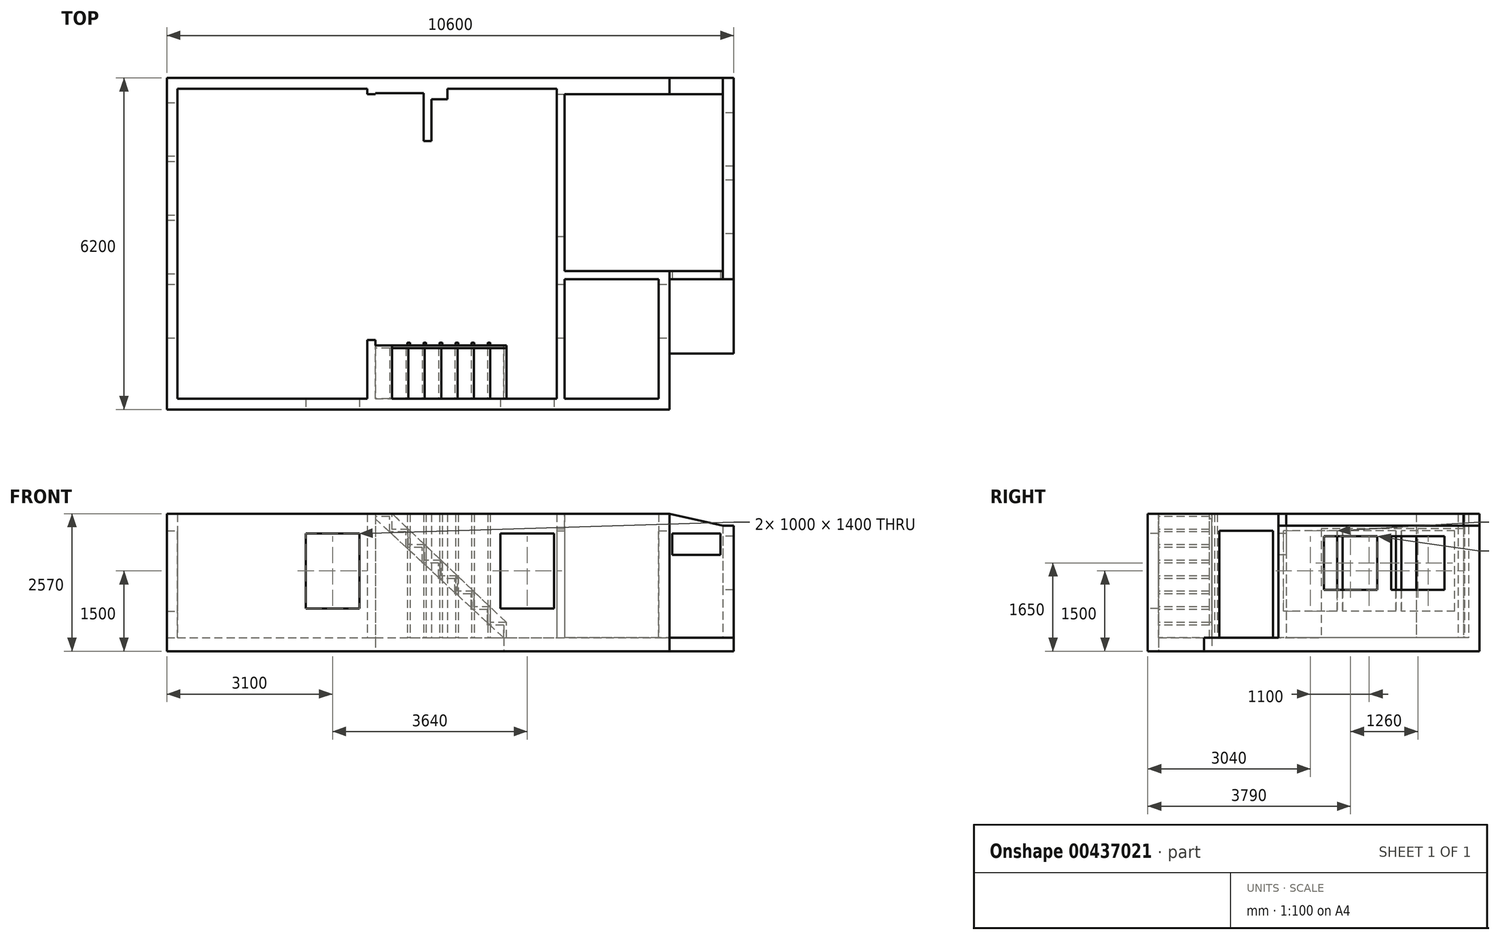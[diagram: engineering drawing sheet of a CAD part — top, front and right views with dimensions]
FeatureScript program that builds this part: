
annotation { "Feature Type Name" : "Feature", "Feature Type Description" : "" }
export const myFeature = defineFeature(function(context is Context, id is Id, definition is map)
    precondition{}
    {
        {
            var Q0;
            Q0=qCreatedBy(makeId("Top.planeOp"),FACE);
            var sketch = newSketch(context, id + "F0", { "sketchPlane" : qUnion([Q0])});
            skLineSegment(sketch, "E0.bottom", {"start": v(0, 0) * mm, "end": v(10600, 0) * mm});
            skLineSegment(sketch, "E0.top", {"start": v(0, -6200) * mm, "end": v(9400, -6200) * mm});
            skLineSegment(sketch, "E0.left", {"start": v(0, 0) * mm, "end": v(0, -6200) * mm});
            skLineSegment(sketch, "E0.right", {"start": v(10600, 0) * mm, "end": v(10600, -5150) * mm});
            skLineSegment(sketch, "E1.top", {"start": v(10600, -5150) * mm, "end": v(9400, -5150) * mm});
            skLineSegment(sketch, "E1.right", {"start": v(9400, -6200) * mm, "end": v(9400, -5150) * mm});
            skLineSegment(sketch, "E2.top", {"start": v(3900, -5000) * mm, "end": v(6300, -5000) * mm});
            skLineSegment(sketch, "E2.left", {"start": v(3900, -6000) * mm, "end": v(3900, -5000) * mm});
            skLineSegment(sketch, "E2.right", {"start": v(6300, -6000) * mm, "end": v(6300, -5000) * mm});
            skLineSegment(sketch, "E3.top", {"start": v(3900, -6000) * mm, "end": v(6300, -6000) * mm});
            skSolve(sketch);
        }
        {
            var Q0;
            Q0=qSketchRegion(id+"F0",true);
            extrude(context, id + "F1", {"entities" : qUnion([Q0]), "depth" : 250 * mm});
        }
        {
            var Q0;
            Q0=makeQuery(id+"F1.opExtrude","CAP_FACE",FACE,{"disambiguationData":[OSD([sQuery(id+"F0.wireOp",EDGE,"E0.bottom"),sQuery(id+"F0.wireOp",EDGE,"E0.top"),sQuery(id+"F0.wireOp",EDGE,"E0.left"),sQuery(id+"F0.wireOp",EDGE,"E0.right")])],"isStart":false});
            var sketch = newSketch(context, id + "F2", { "sketchPlane" : qUnion([Q0])});
            skLineSegment(sketch, "E4.bottom", {"start": v(200, -200) * mm, "end": v(3750, -200) * mm});
            skLineSegment(sketch, "E4.top", {"start": v(200, -6000) * mm, "end": v(3750, -6000) * mm});
            skLineSegment(sketch, "E4.left", {"start": v(200, -200) * mm, "end": v(200, -6000) * mm});
            skLineSegment(sketch, "E4.right", {"start": v(10400, -300) * mm, "end": v(10400, -3610) * mm});
            skLineSegment(sketch, "E5.bottom", {"start": v(9200, -6000) * mm, "end": v(7440, -6000) * mm});
            skLineSegment(sketch, "E5.top", {"start": v(10400, -3610) * mm, "end": v(7440, -3610) * mm});
            skLineSegment(sketch, "E6.top", {"start": v(3750, -4900) * mm, "end": v(3900, -4900) * mm});
            skLineSegment(sketch, "E6.left", {"start": v(3750, -6000) * mm, "end": v(3750, -4900) * mm});
            skLineSegment(sketch, "E6.right", {"start": v(3900, -6000) * mm, "end": v(3900, -4900) * mm});
            skLineSegment(sketch, "E7.top", {"start": v(3750, -300) * mm, "end": v(3900, -300) * mm});
            skLineSegment(sketch, "E7.left", {"start": v(3750, -200) * mm, "end": v(3750, -300) * mm});
            skLineSegment(sketch, "E7.right", {"start": v(3900, -280) * mm, "end": v(3900, -300) * mm});
            skLineSegment(sketch, "E8.top", {"start": v(4800, -1180) * mm, "end": v(4950, -1180) * mm});
            skLineSegment(sketch, "E8.left", {"start": v(4800, -280) * mm, "end": v(4800, -1180) * mm});
            skLineSegment(sketch, "E8.right", {"start": v(4950, -400) * mm, "end": v(4950, -1180) * mm});
            skLineSegment(sketch, "E9.top", {"start": v(7290, -300) * mm, "end": v(7440, -300) * mm});
            skLineSegment(sketch, "E9.left", {"start": v(7290, -200) * mm, "end": v(7290, -300) * mm});
            skLineSegment(sketch, "E10.top", {"start": v(9200, -3760) * mm, "end": v(7440, -3760) * mm});
            skLineSegment(sketch, "E10.right", {"start": v(7440, -6000) * mm, "end": v(7440, -3760) * mm});
            skLineSegment(sketch, "E11.top", {"start": v(7290, -2960) * mm, "end": v(7440, -2960) * mm});
            skLineSegment(sketch, "E11.left", {"start": v(7290, -6000) * mm, "end": v(7290, -2960) * mm});
            skLineSegment(sketch, "E11.right", {"start": v(7440, -3610) * mm, "end": v(7440, -2960) * mm});
            skLineSegment(sketch, "E12.bottom", {"start": v(0, 0) * mm, "end": v(10600, 0) * mm});
            skLineSegment(sketch, "E12.top", {"start": v(0, -6200) * mm, "end": v(9400, -6200) * mm});
            skLineSegment(sketch, "E12.left", {"start": v(0, 0) * mm, "end": v(0, -6200) * mm});
            skLineSegment(sketch, "E12.right", {"start": v(10600, 0) * mm, "end": v(10600, -3760) * mm});
            skLineSegment(sketch, "E13.trimOffspring", {"start": v(5250, -200) * mm, "end": v(7290, -200) * mm});
            skLineSegment(sketch, "E14.trimOffspring", {"start": v(3900, -6000) * mm, "end": v(7290, -6000) * mm});
            skLineSegment(sketch, "E15.top", {"start": v(4950, -400) * mm, "end": v(5250, -400) * mm});
            skLineSegment(sketch, "E15.right", {"start": v(5250, -200) * mm, "end": v(5250, -400) * mm});
            skLineSegment(sketch, "E16.top", {"start": v(3900, -280) * mm, "end": v(4800, -280) * mm});
            skLineSegment(sketch, "E17.trimOffspring", {"start": v(7440, -6000) * mm, "end": v(9200, -6000) * mm});
            skLineSegment(sketch, "E18.trimOffspring", {"start": v(9200, -3760) * mm, "end": v(9200, -6000) * mm});
            skLineSegment(sketch, "E19", {"start": v(10600, -3760) * mm, "end": v(9400, -3760) * mm});
            skLineSegment(sketch, "E20", {"start": v(9400, -3760) * mm, "end": v(9400, -6200) * mm});
            skLineSegment(sketch, "E21", {"start": v(7440, -300) * mm, "end": v(10400, -300) * mm});
            skSolve(sketch);
        }
        {
            var Q0;
            Q0=qSketchRegion(id+"F2",true);
            extrude(context, id + "F3", {"entities" : qUnion([Q0]), "operationType" : NewBodyOperationType.ADD, "depth" : 2320 * mm});
        }
        {
            var Q0;
            Q0=makeQuery(id+"F3.boolean.opBoolean","MERGE",FACE,{"derivedFrom":[makeQuery(id+"F1.opExtrude","SWEPT_FACE",FACE,{"disambiguationData":[OSD([sQuery(id+"F0.wireOp",EDGE,"E1.right")])]}),makeQuery(id+"F3.opExtrude","SWEPT_FACE",FACE,{"disambiguationData":[OSD([sQuery(id+"F2.wireOp",EDGE,"E20")])]})]});
            var sketch = newSketch(context, id + "F4", { "sketchPlane" : qUnion([Q0])});
            skLineSegment(sketch, "E22.bottom", {"start": v(-4860, 250) * mm, "end": v(-3860, 250) * mm});
            skLineSegment(sketch, "E22.top", {"start": v(-4860, 2250) * mm, "end": v(-3860, 2250) * mm});
            skLineSegment(sketch, "E22.left", {"start": v(-4860, 250) * mm, "end": v(-4860, 2250) * mm});
            skLineSegment(sketch, "E22.right", {"start": v(-3860, 250) * mm, "end": v(-3860, 2250) * mm});
            skSolve(sketch);
        }
        {
            var Q0;
            Q0=qSketchRegion(id+"F4",true);
            extrude(context, id + "F5", {"entities" : qUnion([Q0]), "operationType" : NewBodyOperationType.REMOVE, "endBound" : BoundingType.THROUGH_ALL, "oppositeDirection" : true, "depth" : 3000 * mm});
        }
        {
            var Q0;
            Q0=makeQuery(id+"F3.boolean.opBoolean","MERGE",FACE,{"derivedFrom":[makeQuery(id+"F1.opExtrude","SWEPT_FACE",FACE,{"disambiguationData":[OSD([sQuery(id+"F0.wireOp",EDGE,"E0.top")])]}),makeQuery(id+"F3.opExtrude","SWEPT_FACE",FACE,{"disambiguationData":[OSD([sQuery(id+"F2.wireOp",EDGE,"E12.top")])]})]});
            var sketch = newSketch(context, id + "F6", { "sketchPlane" : qUnion([Q0])});
            skLineSegment(sketch, "E23.bottom", {"start": v(7240, 2200) * mm, "end": v(6240, 2200) * mm});
            skLineSegment(sketch, "E23.top", {"start": v(7240, 800) * mm, "end": v(6240, 800) * mm});
            skLineSegment(sketch, "E23.left", {"start": v(7240, 2200) * mm, "end": v(7240, 800) * mm});
            skLineSegment(sketch, "E23.right", {"start": v(6240, 2200) * mm, "end": v(6240, 800) * mm});
            skLineSegment(sketch, "E24.bottom", {"start": v(2600, 2200) * mm, "end": v(3600, 2200) * mm});
            skLineSegment(sketch, "E24.top", {"start": v(2600, 800) * mm, "end": v(3600, 800) * mm});
            skLineSegment(sketch, "E24.left", {"start": v(2600, 2200) * mm, "end": v(2600, 800) * mm});
            skLineSegment(sketch, "E24.right", {"start": v(3600, 2200) * mm, "end": v(3600, 800) * mm});
            skLineSegment(sketch, "E25.bottom", {"start": v(9450, 2200) * mm, "end": v(10350, 2200) * mm});
            skLineSegment(sketch, "E25.top", {"start": v(9450, 1800) * mm, "end": v(10350, 1800) * mm});
            skLineSegment(sketch, "E25.left", {"start": v(9450, 2200) * mm, "end": v(9450, 1800) * mm});
            skLineSegment(sketch, "E25.right", {"start": v(10350, 2200) * mm, "end": v(10350, 1800) * mm});
            skSolve(sketch);
        }
        {
            var Q0;
            Q0=qSketchRegion(id+"F6",true);
            var Q1;
            Q1=makeQuery(id+"F3.opExtrude","SWEPT_FACE",FACE,{"disambiguationData":[OSD([sQuery(id+"F2.wireOp",EDGE,"E9.top"),sQuery(id+"F2.wireOp",EDGE,"E21")])]});
            extrude(context, id + "F7", {"entities" : qUnion([Q0]), "operationType" : NewBodyOperationType.REMOVE, "endBound" : BoundingType.UP_TO_SURFACE, "oppositeDirection" : true, "endBoundEntityFace" : qUnion([Q1]), "depth" : 25 * mm});
        }
        {
            var Q0;
            Q0=makeQuery(id+"F3.opExtrude","SWEPT_FACE",FACE,{"disambiguationData":[OSD([sQuery(id+"F2.wireOp",EDGE,"E4.right")])]});
            var sketch = newSketch(context, id + "F8", { "sketchPlane" : qUnion([Q0])});
            skLineSegment(sketch, "E26.bottom", {"start": v(650, 2150) * mm, "end": v(1650, 2150) * mm});
            skLineSegment(sketch, "E26.top", {"start": v(650, 1150) * mm, "end": v(1650, 1150) * mm});
            skLineSegment(sketch, "E26.left", {"start": v(650, 2150) * mm, "end": v(650, 1150) * mm});
            skLineSegment(sketch, "E26.right", {"start": v(1650, 2150) * mm, "end": v(1650, 1150) * mm});
            skLineSegment(sketch, "E27.bottom", {"start": v(1910, 2150) * mm, "end": v(2910, 2150) * mm});
            skLineSegment(sketch, "E27.top", {"start": v(1910, 1150) * mm, "end": v(2910, 1150) * mm});
            skLineSegment(sketch, "E27.left", {"start": v(1910, 2150) * mm, "end": v(1910, 1150) * mm});
            skLineSegment(sketch, "E27.right", {"start": v(2910, 2150) * mm, "end": v(2910, 1150) * mm});
            skSolve(sketch);
        }
        {
            var Q0;
            Q0=qSketchRegion(id+"F8",true);
            extrude(context, id + "F9", {"entities" : qUnion([Q0]), "operationType" : NewBodyOperationType.REMOVE, "endBound" : BoundingType.UP_TO_NEXT, "oppositeDirection" : true, "depth" : 25 * mm});
        }
        {
            var Q0;
            Q0=makeQuery(id+"F3.opExtrude","SWEPT_FACE",FACE,{"disambiguationData":[OSD([sQuery(id+"F2.wireOp",EDGE,"E4.left")])]});
            var sketch = newSketch(context, id + "F10", { "sketchPlane" : qUnion([Q0])});
            skLineSegment(sketch, "E28.bottom", {"start": v(-3660, 2250) * mm, "end": v(-2660, 2250) * mm});
            skLineSegment(sketch, "E28.top", {"start": v(-3660, 750) * mm, "end": v(-2660, 750) * mm});
            skLineSegment(sketch, "E28.left", {"start": v(-3660, 2250) * mm, "end": v(-3660, 750) * mm});
            skLineSegment(sketch, "E28.right", {"start": v(-2660, 2250) * mm, "end": v(-2660, 750) * mm});
            skLineSegment(sketch, "E29.bottom", {"start": v(-2560, 2250) * mm, "end": v(-1560, 2250) * mm});
            skLineSegment(sketch, "E29.top", {"start": v(-2560, 750) * mm, "end": v(-1560, 750) * mm});
            skLineSegment(sketch, "E29.left", {"start": v(-2560, 2250) * mm, "end": v(-2560, 750) * mm});
            skLineSegment(sketch, "E29.right", {"start": v(-1560, 2250) * mm, "end": v(-1560, 750) * mm});
            skLineSegment(sketch, "E30.bottom", {"start": v(-1460, 2250) * mm, "end": v(-460, 2250) * mm});
            skLineSegment(sketch, "E30.top", {"start": v(-1460, 750) * mm, "end": v(-460, 750) * mm});
            skLineSegment(sketch, "E30.left", {"start": v(-1460, 2250) * mm, "end": v(-1460, 750) * mm});
            skLineSegment(sketch, "E30.right", {"start": v(-460, 2250) * mm, "end": v(-460, 750) * mm});
            skSolve(sketch);
        }
        {
            var Q0;
            Q0=qSketchRegion(id+"F10",true);
            extrude(context, id + "F11", {"entities" : qUnion([Q0]), "operationType" : NewBodyOperationType.REMOVE, "endBound" : BoundingType.UP_TO_NEXT, "oppositeDirection" : true, "depth" : 25 * mm});
        }
        {
            var Q0;
            Q0=makeQuery(id+"F3.opExtrude","CAP_FACE",FACE,{"disambiguationData":[OSD([sQuery(id+"F2.wireOp",EDGE,"E4.bottom"),sQuery(id+"F2.wireOp",EDGE,"E4.top"),sQuery(id+"F2.wireOp",EDGE,"E4.left"),sQuery(id+"F2.wireOp",EDGE,"E4.right"),sQuery(id+"F2.wireOp",EDGE,"E5.top"),sQuery(id+"F2.wireOp",EDGE,"E6.top"),sQuery(id+"F2.wireOp",EDGE,"E6.left"),sQuery(id+"F2.wireOp",EDGE,"E6.right"),sQuery(id+"F2.wireOp",EDGE,"E7.top"),sQuery(id+"F2.wireOp",EDGE,"E7.left"),sQuery(id+"F2.wireOp",EDGE,"E7.right"),sQuery(id+"F2.wireOp",EDGE,"E8.top"),sQuery(id+"F2.wireOp",EDGE,"E8.left"),sQuery(id+"F2.wireOp",EDGE,"E8.right"),sQuery(id+"F2.wireOp",EDGE,"E9.top"),sQuery(id+"F2.wireOp",EDGE,"E9.left"),sQuery(id+"F2.wireOp",EDGE,"E9.right"),sQuery(id+"F2.wireOp",EDGE,"E10.top"),sQuery(id+"F2.wireOp",EDGE,"E10.right"),sQuery(id+"F2.wireOp",EDGE,"E11.top"),sQuery(id+"F2.wireOp",EDGE,"E11.left"),sQuery(id+"F2.wireOp",EDGE,"E11.right"),sQuery(id+"F2.wireOp",EDGE,"E12.bottom"),sQuery(id+"F2.wireOp",EDGE,"E12.top"),sQuery(id+"F2.wireOp",EDGE,"E12.left"),sQuery(id+"F2.wireOp",EDGE,"E12.right"),sQuery(id+"F2.wireOp",EDGE,"E13.trimOffspring"),sQuery(id+"F2.wireOp",EDGE,"f96be5dc-ae23-419c-a534-e8c19ccc8482.trimOffspring"),sQuery(id+"F2.wireOp",EDGE,"E14.trimOffspring"),sQuery(id+"F2.wireOp",EDGE,"E15.top"),sQuery(id+"F2.wireOp",EDGE,"E15.right"),sQuery(id+"F2.wireOp",EDGE,"E16.top"),sQuery(id+"F2.wireOp",EDGE,"E17.trimOffspring"),sQuery(id+"F2.wireOp",EDGE,"E18.trimOffspring"),sQuery(id+"F2.wireOp",EDGE,"E19"),sQuery(id+"F2.wireOp",EDGE,"E20")])],"isStart":false});
            var sketch = newSketch(context, id + "F12", { "sketchPlane" : qUnion([Q0])});
            skLineSegment(sketch, "E31.bottom", {"start": v(7290, -300) * mm, "end": v(7440, -300) * mm});
            skLineSegment(sketch, "E31.top", {"start": v(7290, -2960) * mm, "end": v(7440, -2960) * mm});
            skLineSegment(sketch, "E31.left", {"start": v(7290, -300) * mm, "end": v(7290, -2960) * mm});
            skLineSegment(sketch, "E31.right", {"start": v(7440, -300) * mm, "end": v(7440, -2960) * mm});
            skSolve(sketch);
        }
        {
            var Q0;
            Q0=qSketchRegion(id+"F12",true);
            extrude(context, id + "F13", {"entities" : qUnion([Q0]), "operationType" : NewBodyOperationType.ADD, "oppositeDirection" : true, "depth" : 280 * mm});
        }
        {
            var Q0;
            Q0=makeQuery(id+"F3.boolean.opBoolean","MERGE",FACE,{"derivedFrom":[makeQuery(id+"F1.opExtrude","SWEPT_FACE",FACE,{"disambiguationData":[OSD([sQuery(id+"F0.wireOp",EDGE,"E3.top")])]}),makeQuery(id+"F3.opExtrude","SWEPT_FACE",FACE,{"disambiguationData":[OSD([sQuery(id+"F2.wireOp",EDGE,"E14.trimOffspring")])]})]});
            var sketch = newSketch(context, id + "F14", { "sketchPlane" : qUnion([Q0])});
            skLineSegment(sketch, "E32", {"start": v(-6350, 250) * mm, "end": v(-6350, 540) * mm});
            skLineSegment(sketch, "E33", {"start": v(-6350, 540) * mm, "end": v(-6045, 540) * mm});
            skLineSegment(sketch, "E34", {"start": v(-6045, 540) * mm, "end": v(-6045, 830) * mm});
            skLineSegment(sketch, "E35", {"start": v(-6045, 830) * mm, "end": v(-5740, 830) * mm});
            skLineSegment(sketch, "E36", {"start": v(-5740, 830) * mm, "end": v(-5740, 1120) * mm});
            skLineSegment(sketch, "E37", {"start": v(-5740, 1120) * mm, "end": v(-5435, 1120) * mm});
            skLineSegment(sketch, "E38", {"start": v(-5435, 1120) * mm, "end": v(-5435, 1410) * mm});
            skLineSegment(sketch, "E39", {"start": v(-5435, 1410) * mm, "end": v(-5130, 1410) * mm});
            skLineSegment(sketch, "E40", {"start": v(-5130, 1410) * mm, "end": v(-5130, 1700) * mm});
            skLineSegment(sketch, "E41", {"start": v(-5130, 1700) * mm, "end": v(-4825, 1700) * mm});
            skLineSegment(sketch, "E42", {"start": v(-4825, 1700) * mm, "end": v(-4825, 1990) * mm});
            skLineSegment(sketch, "E43", {"start": v(-4825, 1990) * mm, "end": v(-4520, 1990) * mm});
            skLineSegment(sketch, "E44", {"start": v(-4520, 1990) * mm, "end": v(-4520, 2280) * mm});
            skLineSegment(sketch, "E45", {"start": v(-4520, 2280) * mm, "end": v(-4215, 2280) * mm});
            skLineSegment(sketch, "E46", {"start": v(-4215, 2280) * mm, "end": v(-4215, 2570) * mm});
            skLineSegment(sketch, "E47", {"start": v(-4215, 2570) * mm, "end": v(-3900, 2570) * mm});
            skLineSegment(sketch, "E48.0", {"start": v(-4165, 2520) * mm, "end": v(-3900, 2520) * mm});
            skLineSegment(sketch, "E48.1", {"start": v(-4165, 2230) * mm, "end": v(-4165, 2520) * mm});
            skLineSegment(sketch, "E48.2", {"start": v(-4470, 2230) * mm, "end": v(-4165, 2230) * mm});
            skLineSegment(sketch, "E48.3", {"start": v(-4470, 1940) * mm, "end": v(-4470, 2230) * mm});
            skLineSegment(sketch, "E48.4", {"start": v(-4775, 1940) * mm, "end": v(-4470, 1940) * mm});
            skLineSegment(sketch, "E48.5", {"start": v(-4775, 1650) * mm, "end": v(-4775, 1940) * mm});
            skLineSegment(sketch, "E48.6", {"start": v(-5995, 780) * mm, "end": v(-5690, 780) * mm});
            skLineSegment(sketch, "E48.7", {"start": v(-5995, 490) * mm, "end": v(-5995, 780) * mm});
            skLineSegment(sketch, "E48.8", {"start": v(-6300, 490) * mm, "end": v(-5995, 490) * mm});
            skLineSegment(sketch, "E48.9", {"start": v(-6300, 250) * mm, "end": v(-6300, 490) * mm});
            skLineSegment(sketch, "E48.10", {"start": v(-5690, 780) * mm, "end": v(-5690, 1070) * mm});
            skLineSegment(sketch, "E48.11", {"start": v(-5690, 1070) * mm, "end": v(-5385, 1070) * mm});
            skLineSegment(sketch, "E48.12", {"start": v(-5385, 1070) * mm, "end": v(-5385, 1360) * mm});
            skLineSegment(sketch, "E48.13", {"start": v(-5385, 1360) * mm, "end": v(-5080, 1360) * mm});
            skLineSegment(sketch, "E48.14", {"start": v(-5080, 1360) * mm, "end": v(-5080, 1650) * mm});
            skLineSegment(sketch, "E48.15", {"start": v(-5080, 1650) * mm, "end": v(-4775, 1650) * mm});
            skLineSegment(sketch, "E49", {"start": v(-3900, 2570) * mm, "end": v(-3900, 2520) * mm});
            skLineSegment(sketch, "E50", {"start": v(-6350, 250) * mm, "end": v(-6300, 250) * mm});
            skLineSegment(sketch, "E51", {"start": v(-3900, 2570) * mm, "end": v(-3900, 250) * mm, "construction": true});
            skSolve(sketch);
        }
        {
            var Q0;
            Q0=qSketchRegion(id+"F14",true);
            extrude(context, id + "F15", {"entities" : qUnion([Q0]), "operationType" : NewBodyOperationType.ADD, "depth" : 950 * mm});
        }
        {
            var Q0;
            Q0=makeQuery(id+"F15.opExtrude","CAP_FACE",FACE,{"disambiguationData":[OSD([sQuery(id+"F14.wireOp",EDGE,"E32"),sQuery(id+"F14.wireOp",EDGE,"E33"),sQuery(id+"F14.wireOp",EDGE,"E34"),sQuery(id+"F14.wireOp",EDGE,"E35"),sQuery(id+"F14.wireOp",EDGE,"E36"),sQuery(id+"F14.wireOp",EDGE,"E37"),sQuery(id+"F14.wireOp",EDGE,"E38"),sQuery(id+"F14.wireOp",EDGE,"E39"),sQuery(id+"F14.wireOp",EDGE,"E40"),sQuery(id+"F14.wireOp",EDGE,"E41"),sQuery(id+"F14.wireOp",EDGE,"E42"),sQuery(id+"F14.wireOp",EDGE,"E43"),sQuery(id+"F14.wireOp",EDGE,"E44"),sQuery(id+"F14.wireOp",EDGE,"E45"),sQuery(id+"F14.wireOp",EDGE,"E46"),sQuery(id+"F14.wireOp",EDGE,"E47"),sQuery(id+"F14.wireOp",EDGE,"E48.0"),sQuery(id+"F14.wireOp",EDGE,"E48.1"),sQuery(id+"F14.wireOp",EDGE,"E48.2"),sQuery(id+"F14.wireOp",EDGE,"E48.3"),sQuery(id+"F14.wireOp",EDGE,"E48.4"),sQuery(id+"F14.wireOp",EDGE,"E48.5"),sQuery(id+"F14.wireOp",EDGE,"E48.6"),sQuery(id+"F14.wireOp",EDGE,"E48.7"),sQuery(id+"F14.wireOp",EDGE,"E48.8"),sQuery(id+"F14.wireOp",EDGE,"E48.9"),sQuery(id+"F14.wireOp",EDGE,"E48.10"),sQuery(id+"F14.wireOp",EDGE,"E48.11"),sQuery(id+"F14.wireOp",EDGE,"E48.12"),sQuery(id+"F14.wireOp",EDGE,"E48.13"),sQuery(id+"F14.wireOp",EDGE,"E48.14"),sQuery(id+"F14.wireOp",EDGE,"E48.15"),sQuery(id+"F14.wireOp",EDGE,"E49"),sQuery(id+"F14.wireOp",EDGE,"E50")])],"isStart":false});
            var sketch = newSketch(context, id + "F16", { "sketchPlane" : qUnion([Q0])});
            skLineSegment(sketch, "E52", {"start": v(-6350, 540) * mm, "end": v(-4215, 2570) * mm});
            skLineSegment(sketch, "E53", {"start": v(-3900, 2570) * mm, "end": v(-3900, 2475.76) * mm});
            skLineSegment(sketch, "E54", {"start": v(-6300, 250) * mm, "end": v(-4165, 2230) * mm});
            skLineSegment(sketch, "E55", {"start": v(-4165, 2230) * mm, "end": v(-3900, 2475.76) * mm});
            skLineSegment(sketch, "E56", {"start": v(-6350, 540) * mm, "end": v(-6350, 250) * mm});
            skLineSegment(sketch, "E57", {"start": v(-6350, 250) * mm, "end": v(-6300, 250) * mm});
            skLineSegment(sketch, "E58", {"start": v(-4215, 2570) * mm, "end": v(-3900, 2570) * mm});
            skSolve(sketch);
        }
        {
            var Q0;
            Q0=qSketchRegion(id+"F16",true);
            extrude(context, id + "F17", {"entities" : qUnion([Q0]), "operationType" : NewBodyOperationType.ADD, "depth" : 50 * mm});
        }
        {
            var Q0;
            {var subQ0=sQuery(id+"F0.wireOp",EDGE,"E3.top");var subQ1=sQuery(id+"F0.wireOp",EDGE,"E2.right");var subQ2=sQuery(id+"F0.wireOp",EDGE,"E2.left");var subQ3=sQuery(id+"F0.wireOp",EDGE,"E2.top");var subQ4=sQuery(id+"F0.wireOp",EDGE,"E1.right");var subQ5=sQuery(id+"F0.wireOp",EDGE,"E1.top");var subQ6=sQuery(id+"F0.wireOp",EDGE,"E0.right");var subQ7=makeQuery(id+"F1.opExtrude","CAP_FACE",FACE,{"disambiguationData":[OSD([sQuery(id+"F0.wireOp",EDGE,"E0.bottom"),sQuery(id+"F0.wireOp",EDGE,"E0.top"),sQuery(id+"F0.wireOp",EDGE,"E0.left"),subQ6,subQ5,subQ4,subQ3,subQ2,subQ1,subQ0])],"isStart":false});Q0=makeQuery(id+"F5.boolean.opBoolean","MERGE",FACE,{"derivedFrom":[makeQuery(id+"F3.boolean.opBoolean","SPLIT",FACE,{"disambiguationData":[TD([makeQuery(id+"F1.opExtrude","SWEPT_FACE",FACE,{"disambiguationData":[OSD([subQ6])]})])],"derivedFrom":subQ7}),makeQuery(id+"F3.boolean.opBoolean","SPLIT",FACE,{"disambiguationData":[TD([makeQuery(id+"F1.opExtrude","SWEPT_FACE",FACE,{"disambiguationData":[OSD([subQ3])]})])],"derivedFrom":subQ7}),makeQuery(id+"F3.boolean.opBoolean","SPLIT",FACE,{"disambiguationData":[TD([makeQuery(id+"F3.opExtrude","SWEPT_FACE",FACE,{"disambiguationData":[OSD([sQuery(id+"F2.wireOp",EDGE,"E10.top")])]})])],"derivedFrom":subQ7}),makeQuery(id+"F5.opExtrude","SWEPT_FACE",FACE,{"disambiguationData":[OSD([sQuery(id+"F4.wireOp",EDGE,"E22.bottom")])]})]});}
            var sketch = newSketch(context, id + "F18", { "sketchPlane" : qUnion([Q0])});
            skLineSegment(sketch, "E59.bottom", {"start": v(6045, -5000) * mm, "end": v(6005, -5000) * mm});
            skLineSegment(sketch, "E59.top", {"start": v(6045, -4950) * mm, "end": v(6005, -4950) * mm});
            skLineSegment(sketch, "E59.left", {"start": v(6050, -4995) * mm, "end": v(6050, -4955) * mm});
            skLineSegment(sketch, "E59.right", {"start": v(6000, -4995) * mm, "end": v(6000, -4955) * mm});
            skPoint(sketch, "E60.visualSharp", {"position": v(6000, -4950) * mm});
            skArc(sketch, "E60.filletArc", {"start": v(6005, -4950) * mm, "mid": v(6001.46, -4951.46) * mm, "end": v(6000, -4955) * mm});
            skPoint(sketch, "E61.visualSharp", {"position": v(6050, -4950) * mm});
            skArc(sketch, "E61.filletArc", {"start": v(6050, -4955) * mm, "mid": v(6048.54, -4951.46) * mm, "end": v(6045, -4950) * mm});
            skPoint(sketch, "E62.visualSharp", {"position": v(6050, -5000) * mm});
            skArc(sketch, "E62.filletArc", {"start": v(6045, -5000) * mm, "mid": v(6048.54, -4998.54) * mm, "end": v(6050, -4995) * mm});
            skPoint(sketch, "E63.visualSharp", {"position": v(6000, -5000) * mm});
            skArc(sketch, "E63.filletArc", {"start": v(6000, -4995) * mm, "mid": v(6001.46, -4998.54) * mm, "end": v(6005, -5000) * mm});
            skPoint(sketch, "E64.1.0.0", {"position": v(5700, -5000) * mm});
            skLineSegment(sketch, "E64.1.0.1", {"start": v(5745, -5000) * mm, "end": v(5705, -5000) * mm});
            skLineSegment(sketch, "E64.1.0.2", {"start": v(5745, -4950) * mm, "end": v(5705, -4950) * mm});
            skPoint(sketch, "E64.1.0.3", {"position": v(5700, -4950) * mm});
            skLineSegment(sketch, "E64.1.0.4", {"start": v(5750, -4995) * mm, "end": v(5750, -4955) * mm});
            skPoint(sketch, "E64.1.0.5", {"position": v(5750, -4950) * mm});
            skPoint(sketch, "E64.1.0.6", {"position": v(5750, -5000) * mm});
            skLineSegment(sketch, "E64.1.0.7", {"start": v(5700, -4995) * mm, "end": v(5700, -4955) * mm});
            skArc(sketch, "E64.1.0.8", {"start": v(5750, -4955) * mm, "mid": v(5748.54, -4951.46) * mm, "end": v(5745, -4950) * mm});
            skArc(sketch, "E64.1.0.9", {"start": v(5705, -4950) * mm, "mid": v(5701.46, -4951.46) * mm, "end": v(5700, -4955) * mm});
            skArc(sketch, "E64.1.0.10", {"start": v(5700, -4995) * mm, "mid": v(5701.46, -4998.54) * mm, "end": v(5705, -5000) * mm});
            skArc(sketch, "E64.1.0.11", {"start": v(5745, -5000) * mm, "mid": v(5748.54, -4998.54) * mm, "end": v(5750, -4995) * mm});
            skPoint(sketch, "E64.2.0.0", {"position": v(5400, -5000) * mm});
            skLineSegment(sketch, "E64.2.0.1", {"start": v(5445, -5000) * mm, "end": v(5405, -5000) * mm});
            skLineSegment(sketch, "E64.2.0.2", {"start": v(5445, -4950) * mm, "end": v(5405, -4950) * mm});
            skPoint(sketch, "E64.2.0.3", {"position": v(5400, -4950) * mm});
            skLineSegment(sketch, "E64.2.0.4", {"start": v(5450, -4995) * mm, "end": v(5450, -4955) * mm});
            skPoint(sketch, "E64.2.0.5", {"position": v(5450, -4950) * mm});
            skPoint(sketch, "E64.2.0.6", {"position": v(5450, -5000) * mm});
            skLineSegment(sketch, "E64.2.0.7", {"start": v(5400, -4995) * mm, "end": v(5400, -4955) * mm});
            skArc(sketch, "E64.2.0.8", {"start": v(5450, -4955) * mm, "mid": v(5448.54, -4951.46) * mm, "end": v(5445, -4950) * mm});
            skArc(sketch, "E64.2.0.9", {"start": v(5405, -4950) * mm, "mid": v(5401.46, -4951.46) * mm, "end": v(5400, -4955) * mm});
            skArc(sketch, "E64.2.0.10", {"start": v(5400, -4995) * mm, "mid": v(5401.46, -4998.54) * mm, "end": v(5405, -5000) * mm});
            skArc(sketch, "E64.2.0.11", {"start": v(5445, -5000) * mm, "mid": v(5448.54, -4998.54) * mm, "end": v(5450, -4995) * mm});
            skPoint(sketch, "E64.3.0.0", {"position": v(5100, -5000) * mm});
            skLineSegment(sketch, "E64.3.0.1", {"start": v(5145, -5000) * mm, "end": v(5105, -5000) * mm});
            skLineSegment(sketch, "E64.3.0.2", {"start": v(5145, -4950) * mm, "end": v(5105, -4950) * mm});
            skPoint(sketch, "E64.3.0.3", {"position": v(5100, -4950) * mm});
            skLineSegment(sketch, "E64.3.0.4", {"start": v(5150, -4995) * mm, "end": v(5150, -4955) * mm});
            skPoint(sketch, "E64.3.0.5", {"position": v(5150, -4950) * mm});
            skPoint(sketch, "E64.3.0.6", {"position": v(5150, -5000) * mm});
            skLineSegment(sketch, "E64.3.0.7", {"start": v(5100, -4995) * mm, "end": v(5100, -4955) * mm});
            skArc(sketch, "E64.3.0.8", {"start": v(5150, -4955) * mm, "mid": v(5148.54, -4951.46) * mm, "end": v(5145, -4950) * mm});
            skArc(sketch, "E64.3.0.9", {"start": v(5105, -4950) * mm, "mid": v(5101.46, -4951.46) * mm, "end": v(5100, -4955) * mm});
            skArc(sketch, "E64.3.0.10", {"start": v(5100, -4995) * mm, "mid": v(5101.46, -4998.54) * mm, "end": v(5105, -5000) * mm});
            skArc(sketch, "E64.3.0.11", {"start": v(5145, -5000) * mm, "mid": v(5148.54, -4998.54) * mm, "end": v(5150, -4995) * mm});
            skPoint(sketch, "E64.4.0.0", {"position": v(4800, -5000) * mm});
            skLineSegment(sketch, "E64.4.0.1", {"start": v(4845, -5000) * mm, "end": v(4805, -5000) * mm});
            skLineSegment(sketch, "E64.4.0.2", {"start": v(4845, -4950) * mm, "end": v(4805, -4950) * mm});
            skPoint(sketch, "E64.4.0.3", {"position": v(4800, -4950) * mm});
            skLineSegment(sketch, "E64.4.0.4", {"start": v(4850, -4995) * mm, "end": v(4850, -4955) * mm});
            skPoint(sketch, "E64.4.0.5", {"position": v(4850, -4950) * mm});
            skPoint(sketch, "E64.4.0.6", {"position": v(4850, -5000) * mm});
            skLineSegment(sketch, "E64.4.0.7", {"start": v(4800, -4995) * mm, "end": v(4800, -4955) * mm});
            skArc(sketch, "E64.4.0.8", {"start": v(4850, -4955) * mm, "mid": v(4848.54, -4951.46) * mm, "end": v(4845, -4950) * mm});
            skArc(sketch, "E64.4.0.9", {"start": v(4805, -4950) * mm, "mid": v(4801.46, -4951.46) * mm, "end": v(4800, -4955) * mm});
            skArc(sketch, "E64.4.0.10", {"start": v(4800, -4995) * mm, "mid": v(4801.46, -4998.54) * mm, "end": v(4805, -5000) * mm});
            skArc(sketch, "E64.4.0.11", {"start": v(4845, -5000) * mm, "mid": v(4848.54, -4998.54) * mm, "end": v(4850, -4995) * mm});
            skPoint(sketch, "E64.5.0.0", {"position": v(4500, -5000) * mm});
            skLineSegment(sketch, "E64.5.0.1", {"start": v(4545, -5000) * mm, "end": v(4505, -5000) * mm});
            skLineSegment(sketch, "E64.5.0.2", {"start": v(4545, -4950) * mm, "end": v(4505, -4950) * mm});
            skPoint(sketch, "E64.5.0.3", {"position": v(4500, -4950) * mm});
            skLineSegment(sketch, "E64.5.0.4", {"start": v(4550, -4995) * mm, "end": v(4550, -4955) * mm});
            skPoint(sketch, "E64.5.0.5", {"position": v(4550, -4950) * mm});
            skPoint(sketch, "E64.5.0.6", {"position": v(4550, -5000) * mm});
            skLineSegment(sketch, "E64.5.0.7", {"start": v(4500, -4995) * mm, "end": v(4500, -4955) * mm});
            skArc(sketch, "E64.5.0.8", {"start": v(4550, -4955) * mm, "mid": v(4548.54, -4951.46) * mm, "end": v(4545, -4950) * mm});
            skArc(sketch, "E64.5.0.9", {"start": v(4505, -4950) * mm, "mid": v(4501.46, -4951.46) * mm, "end": v(4500, -4955) * mm});
            skArc(sketch, "E64.5.0.10", {"start": v(4500, -4995) * mm, "mid": v(4501.46, -4998.54) * mm, "end": v(4505, -5000) * mm});
            skArc(sketch, "E64.5.0.11", {"start": v(4545, -5000) * mm, "mid": v(4548.54, -4998.54) * mm, "end": v(4550, -4995) * mm});
            skLineSegment(sketch, "E64.direction1", {"start": v(6000, -5000) * mm, "end": v(5700, -5000) * mm, "construction": true});
            skSolve(sketch);
        }
        {
            var Q0;
            Q0=qSketchRegion(id+"F18",true);
            extrude(context, id + "F19", {"entities" : qUnion([Q0]), "operationType" : NewBodyOperationType.ADD, "depth" : 2320 * mm});
        }
        {
            var Q0;
            Q0=makeQuery(id+"F3.opExtrude","SWEPT_FACE",FACE,{"disambiguationData":[OSD([sQuery(id+"F2.wireOp",EDGE,"E19")])]});
            var sketch = newSketch(context, id + "F20", { "sketchPlane" : qUnion([Q0])});
            skLineSegment(sketch, "E65", {"start": v(9400, 2570) * mm, "end": v(10400, 2350) * mm});
            skLineSegment(sketch, "E66", {"start": v(10400, 2350) * mm, "end": v(10600, 2350) * mm});
            skLineSegment(sketch, "E67", {"start": v(10600, 2350) * mm, "end": v(10600, 2570) * mm});
            skLineSegment(sketch, "E68", {"start": v(10600, 2570) * mm, "end": v(9400, 2570) * mm});
            skSolve(sketch);
        }
        {
            var Q0;
            Q0 = qSketchRegion(id + "F20", true);
            extrude(context, id + "F21", {"entities" : qUnion([Q0]), "operationType" : NewBodyOperationType.REMOVE, "endBound" : BoundingType.THROUGH_ALL, "oppositeDirection" : true, "depth" : 25 * mm});
        }
    });
